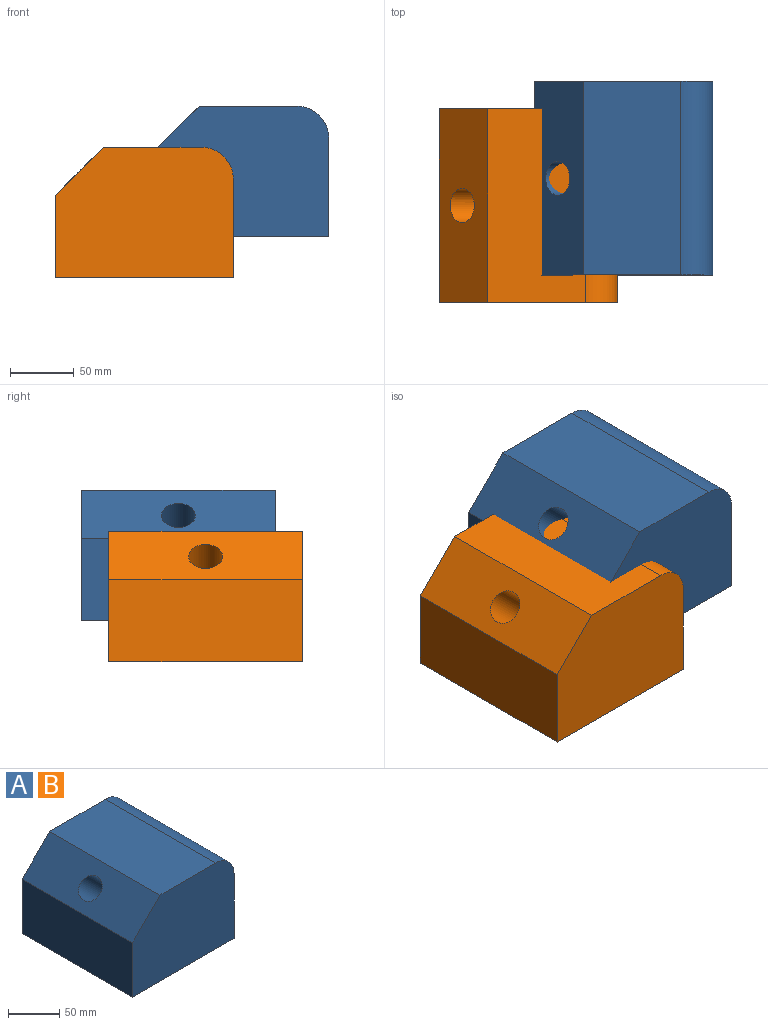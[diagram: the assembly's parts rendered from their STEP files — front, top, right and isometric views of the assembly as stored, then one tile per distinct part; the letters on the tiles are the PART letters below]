
ASSEMBLY  parts=2 mates=1
PART A: 10 faces, bbox 140x151.9x102.6 mm
  f0: plane 151.89x76.53mm, normal (0,0,1), area 11623.8mm2, adj f4,f5,f6,f7
  f1: plane 151.89x64.54mm, normal (-1,0,0), area 9803.7mm2, adj f2,f5,f6,f7
  f2: plane 151.89x140.03mm, normal (0,0,-1), area 21268.9mm2, adj f1,f3,f5,f6
  f3: plane 151.89x77.24mm, normal (1,0,0), area 11732.7mm2, adj f2,f4,f5,f6
  f4: cylinder r=25.4mm len=151.89mm, axis (0,1,0), area 6060.2mm2, adj f0,f3,f5,f6
  f5: plane 140.03x102.64mm, normal (0,-1,0), area 13508.6mm2, adj f0,f1,f2,f3,f4,f7
  f6: plane 140.03x102.64mm, normal (0,1,0), area 13508.6mm2, adj f0,f1,f2,f3,f4,f7
  f7: plane 151.89x38.1mm, normal (-0.71,0,0.71), area 7625.3mm2, adj f0,f1,f5,f6,f8
  f8: cylinder r=13.34mm len=64.84mm, axis (-0.71,0,0.71), area 5449.1mm2, adj f7,f9
  f9: plane 26.67x18.86mm, normal (-0.71,0,0.71), area 558.8mm2, adj f8
PART B: same geometry as A
PLACE A t=(7.79,38.85,4.57)mm
PLACE B t=(-67.14,17.48,-27.59)mm
MATE parallel A.f5 <-> B.f4  axis (0,-1,0) through (80.23,-37.1,53.35)mm
